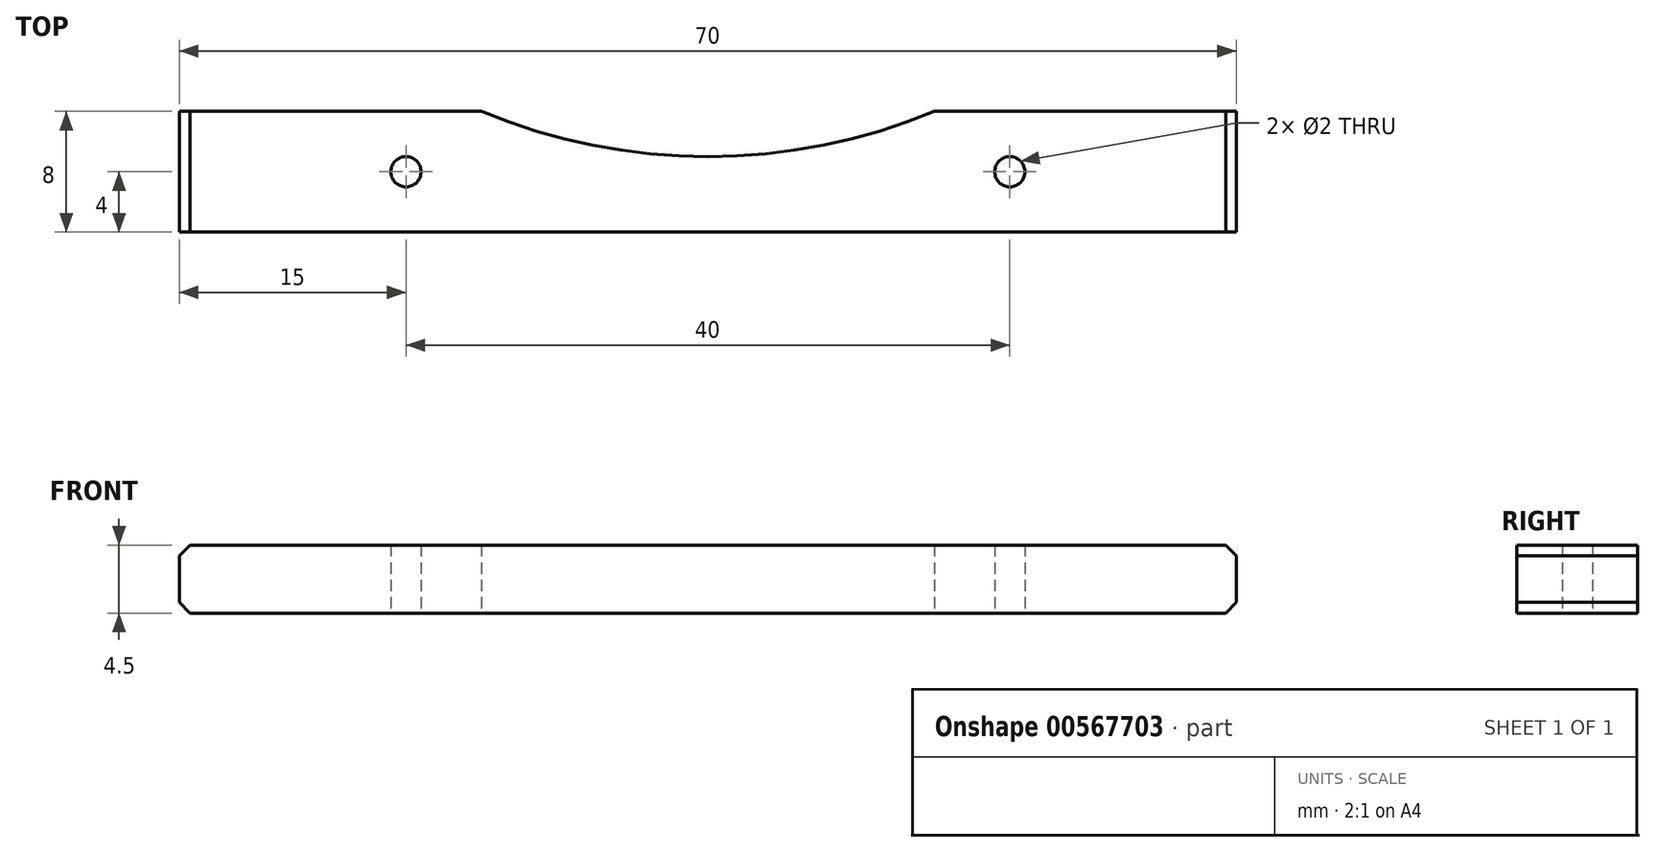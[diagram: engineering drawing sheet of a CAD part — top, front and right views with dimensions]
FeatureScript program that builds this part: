
annotation { "Feature Type Name" : "Feature", "Feature Type Description" : "" }
export const myFeature = defineFeature(function(context is Context, id is Id, definition is map)
    precondition{}
    {
        {
            var Q0;
            Q0=qCreatedBy(makeId("Top.planeOp"),FACE);
            var sketch = newSketch(context, id + "F0", { "sketchPlane" : qUnion([Q0])});
            skLineSegment(sketch, "E0.bottom", {"start": v(35, -4) * mm, "end": v(-35, -4) * mm});
            skLineSegment(sketch, "E0.top", {"start": v(35, 4) * mm, "end": v(15, 4) * mm});
            skLineSegment(sketch, "E0.left", {"start": v(35, -4) * mm, "end": v(35, 4) * mm});
            skLineSegment(sketch, "E0.right", {"start": v(-35, -4) * mm, "end": v(-35, 4) * mm});
            skPoint(sketch, "E0.middle", {"position": v(0, 0) * mm});
            skLineSegment(sketch, "E1", {"start": v(-35, 4) * mm, "end": v(-15, 4) * mm});
            skLineSegment(sketch, "E2", {"start": v(0, 0) * mm, "end": v(0, 1) * mm});
            skArc(sketch, "E3", {"start": v(-15, 4) * mm, "mid": v(0, 1) * mm, "end": v(15, 4) * mm});
            skLineSegment(sketch, "E4.trimOffspring", {"start": v(-15, 4) * mm, "end": v(-35, 4) * mm});
            skLineSegment(sketch, "E5", {"start": v(0, 0) * mm, "end": v(20, 0) * mm});
            skLineSegment(sketch, "E6", {"start": v(0, 0) * mm, "end": v(-20, 0) * mm});
            skCircle(sketch, "E7", {"center": v(-20, 0) * mm, "radius": 1 * mm});
            skCircle(sketch, "E8", {"center": v(20, 0) * mm, "radius": 1 * mm});
            skSolve(sketch);
        }
        {
            var Q0;
            Q0=makeQuery(id+"F0.imprint","IMPRINT",FACE,{"disambiguationData":[TD([[makeQuery(id+"F0.imprint","IMPRINT",EDGE,{"derivedFrom":sQuery(id+"F0.wireOp",EDGE,"E0.bottom")}),-1.0]])]});
            extrude(context, id + "F1", {"entities" : qUnion([Q0]), "depth" : 4.5 * mm, "offsetDistance" : 25 * mm});
        }
        {
            var Q0;
            Q0=makeQuery(id+"F1.opExtrude","CAP_EDGE",EDGE,{"disambiguationData":[OSD([sQuery(id+"F0.wireOp",EDGE,"E0.right")])],"isStart":false});
            var Q1;
            Q1=makeQuery(id+"F1.opExtrude","CAP_EDGE",EDGE,{"disambiguationData":[OSD([sQuery(id+"F0.wireOp",EDGE,"E0.left")])],"isStart":false});
            var Q2;
            Q2=makeQuery(id+"F1.opExtrude","CAP_EDGE",EDGE,{"disambiguationData":[OSD([sQuery(id+"F0.wireOp",EDGE,"E0.right")])],"isStart":true});
            var Q3;
            Q3=makeQuery(id+"F1.opExtrude","CAP_EDGE",EDGE,{"disambiguationData":[OSD([sQuery(id+"F0.wireOp",EDGE,"E0.left")])],"isStart":true});
            chamfer(context, id + "F2", {"entities" : qUnion([Q0, Q1, Q2, Q3]), "width" : 0.7 * mm, "tangentPropagation" : true});
        }
    });
